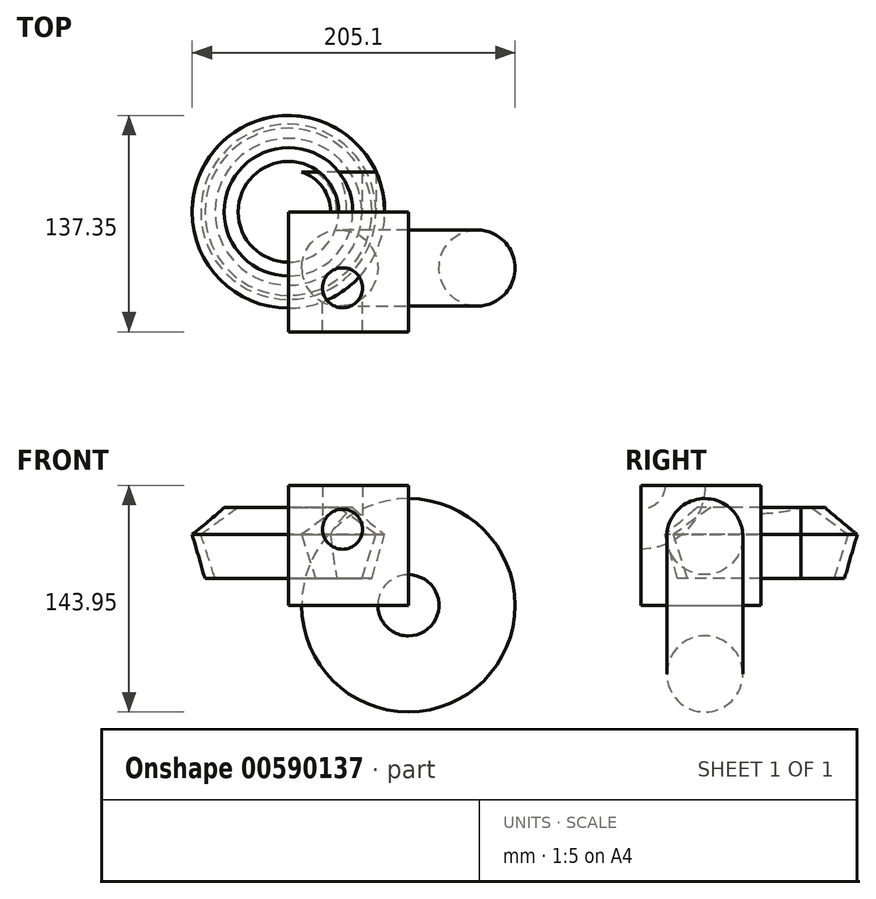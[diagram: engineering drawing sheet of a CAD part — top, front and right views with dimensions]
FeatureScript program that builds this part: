
annotation { "Feature Type Name" : "Feature", "Feature Type Description" : "" }
export const myFeature = defineFeature(function(context is Context, id is Id, definition is map)
    precondition{}
    {
        {
            var Q0;
            Q0=qCreatedBy(makeId("Front.planeOp"),FACE);
            var sketch = newSketch(context, id + "F0", { "sketchPlane" : qUnion([Q0])});
            skLineSegment(sketch, "E0.bottom", {"start": v(0, 0) * mm, "end": v(76.2, 0) * mm});
            skLineSegment(sketch, "E0.top", {"start": v(0, 76.2) * mm, "end": v(76.2, 76.2) * mm});
            skLineSegment(sketch, "E0.left", {"start": v(0, 0) * mm, "end": v(0, 76.2) * mm});
            skLineSegment(sketch, "E0.right", {"start": v(76.2, 0) * mm, "end": v(76.2, 76.2) * mm});
            skSolve(sketch);
        }
        {
            var Q0;
            Q0 = qSketchRegion(id + "F0", true);
            extrude(context, id + "F1", {"entities" : qUnion([Q0]), "depth" : 76.2 * mm, "offsetDistance" : 25.4 * mm});
        }
        {
            var Q0;
            Q0=makeQuery(id+"F1.opExtrude","CAP_FACE",FACE,{"disambiguationData":[OSD([sQuery(id+"F0.wireOp",EDGE,"E0.bottom"),sQuery(id+"F0.wireOp",EDGE,"E0.top"),sQuery(id+"F0.wireOp",EDGE,"E0.left"),sQuery(id+"F0.wireOp",EDGE,"E0.right")])],"isStart":false});
            var sketch = newSketch(context, id + "F2", { "sketchPlane" : qUnion([Q0])});
            skCircle(sketch, "E1", {"center": v(34.4, 48.27) * mm, "radius": 12.7 * mm});
            skSolve(sketch);
        }
        {
            var Q0;
            Q0 = qSketchRegion(id + "F2", true);
            var Q1;
            Q1=makeQuery(id+"F1.opExtrude","CAP_EDGE",EDGE,{"disambiguationData":[OSD([sQuery(id+"F0.wireOp",EDGE,"E0.top")])],"isStart":false});
            revolve(context, id + "F3", {"entities" : qUnion([Q0]), "axis" : qUnion([Q1]), "revolveType" : RevolveType.FULL});
        }
        {
            var Q0;
            Q0=makeQuery(id+"F1.opExtrude","SWEPT_FACE",FACE,{"disambiguationData":[OSD([sQuery(id+"F0.wireOp",EDGE,"E0.right")])]});
            var sketch = newSketch(context, id + "F4", { "sketchPlane" : qUnion([Q0])});
            skCircle(sketch, "E2", {"center": v(-35.67, 43.6) * mm, "radius": 24.16 * mm});
            skSolve(sketch);
        }
        {
            var Q0;
            Q0 = qSketchRegion(id + "F4", true);
            var Q1;
            Q1=makeQuery(id+"F1.opExtrude","SWEPT_EDGE",EDGE,{"disambiguationData":[OSD([sQuery(id+"F0.wireOp",EDGE,"E0.bottom"),sQuery(id+"F0.wireOp",EDGE,"E0.right")])]});
            revolve(context, id + "F5", {"entities" : qUnion([Q0]), "axis" : qUnion([Q1]), "revolveType" : RevolveType.FULL});
        }
        {
            var Q0;
            Q0=makeQuery(id+"F3.opRevolve","SWEPT_BODY",BODY,{"disambiguationData":[OSD([sQuery(id+"F2.wireOp",EDGE,"E1")])]});
            var Q1;
            Q1=makeQuery(id+"F1.opExtrude","SWEPT_BODY",BODY,{"disambiguationData":[OSD([sQuery(id+"F0.wireOp",EDGE,"E0.bottom"),sQuery(id+"F0.wireOp",EDGE,"E0.top"),sQuery(id+"F0.wireOp",EDGE,"E0.left"),sQuery(id+"F0.wireOp",EDGE,"E0.right")])]});
            booleanBodies(context, id + "F6", {"operationType" : BooleanOperationType.SUBTRACTION, "tools" : qUnion([Q0]), "targets" : qUnion([Q1])});
        }
        {
            var Q0;
            Q0=makeQuery(id+"F1.opExtrude","CAP_FACE",FACE,{"disambiguationData":[OSD([sQuery(id+"F0.wireOp",EDGE,"E0.bottom"),sQuery(id+"F0.wireOp",EDGE,"E0.top"),sQuery(id+"F0.wireOp",EDGE,"E0.left"),sQuery(id+"F0.wireOp",EDGE,"E0.right")])],"isStart":true});
            var sketch = newSketch(context, id + "F7", { "sketchPlane" : qUnion([Q0])});
            skCircle(sketch, "E3.cCircle", {"center": v(-31.95, 37.2) * mm, "radius": 20.14 * mm, "construction": true});
            skLineSegment(sketch, "E3.0", {"start": v(-17.32, 17.06) * mm, "end": v(-46.58, 17.06) * mm});
            skLineSegment(sketch, "E3.1", {"start": v(-46.58, 17.06) * mm, "end": v(-55.63, 44.89) * mm});
            skLineSegment(sketch, "E3.2", {"start": v(-55.63, 44.89) * mm, "end": v(-31.95, 62.09) * mm});
            skLineSegment(sketch, "E3.3", {"start": v(-31.95, 62.09) * mm, "end": v(-8.28, 44.89) * mm});
            skLineSegment(sketch, "E3.4", {"start": v(-8.28, 44.89) * mm, "end": v(-17.32, 17.06) * mm});
            skPoint(sketch, "E3.0.midPoint", {"position": v(-31.95, 17.06) * mm});
            skSolve(sketch);
        }
        {
            var Q0;
            Q0 = qSketchRegion(id + "F7", true);
            extrude(context, id + "F8", {"entities" : qUnion([Q0]), "depth" : 25.4 * mm, "offsetDistance" : 25.4 * mm});
        }
        {
            var Q0;
            Q0=makeQuery(id+"F8.opExtrude","SWEPT_FACE",FACE,{"disambiguationData":[OSD([sQuery(id+"F7.wireOp",EDGE,"E3.1")])]});
            var Q1;
            Q1=makeQuery(id+"F8.opExtrude","CAP_FACE",FACE,{"disambiguationData":[OSD([sQuery(id+"F7.wireOp",EDGE,"E3.0"),sQuery(id+"F7.wireOp",EDGE,"E3.1"),sQuery(id+"F7.wireOp",EDGE,"E3.2"),sQuery(id+"F7.wireOp",EDGE,"E3.3"),sQuery(id+"F7.wireOp",EDGE,"E3.4")])],"isStart":false});
            var Q2;
            Q2=makeQuery(id+"F8.opExtrude","SWEPT_FACE",FACE,{"disambiguationData":[OSD([sQuery(id+"F7.wireOp",EDGE,"E3.2")])]});
            var Q3;
            Q3=makeQuery(id+"F1.opExtrude","CAP_EDGE",EDGE,{"disambiguationData":[OSD([sQuery(id+"F0.wireOp",EDGE,"E0.left")])],"isStart":true});
            revolve(context, id + "F9", {"entities" : qUnion([Q0, Q1, Q2]), "axis" : qUnion([Q3]), "revolveType" : RevolveType.FULL});
        }
        {
            var Q0;
            Q0=makeQuery(id+"F9.opRevolve","SWEPT_BODY",BODY,{"disambiguationData":[OSD([sQuery(id+"F7.wireOp",EDGE,"E3.0"),sQuery(id+"F7.wireOp",EDGE,"E3.1"),sQuery(id+"F7.wireOp",EDGE,"E3.2"),sQuery(id+"F7.wireOp",EDGE,"E3.3"),sQuery(id+"F7.wireOp",EDGE,"E3.4")])]});
            var Q1;
            Q1=makeQuery(id+"F8.opExtrude","SWEPT_BODY",BODY,{"disambiguationData":[OSD([sQuery(id+"F7.wireOp",EDGE,"E3.0"),sQuery(id+"F7.wireOp",EDGE,"E3.1"),sQuery(id+"F7.wireOp",EDGE,"E3.2"),sQuery(id+"F7.wireOp",EDGE,"E3.3"),sQuery(id+"F7.wireOp",EDGE,"E3.4")])]});
            booleanBodies(context, id + "F10", {"operationType" : BooleanOperationType.INTERSECTION, "tools" : qUnion([Q0, Q1])});
        }
    });
